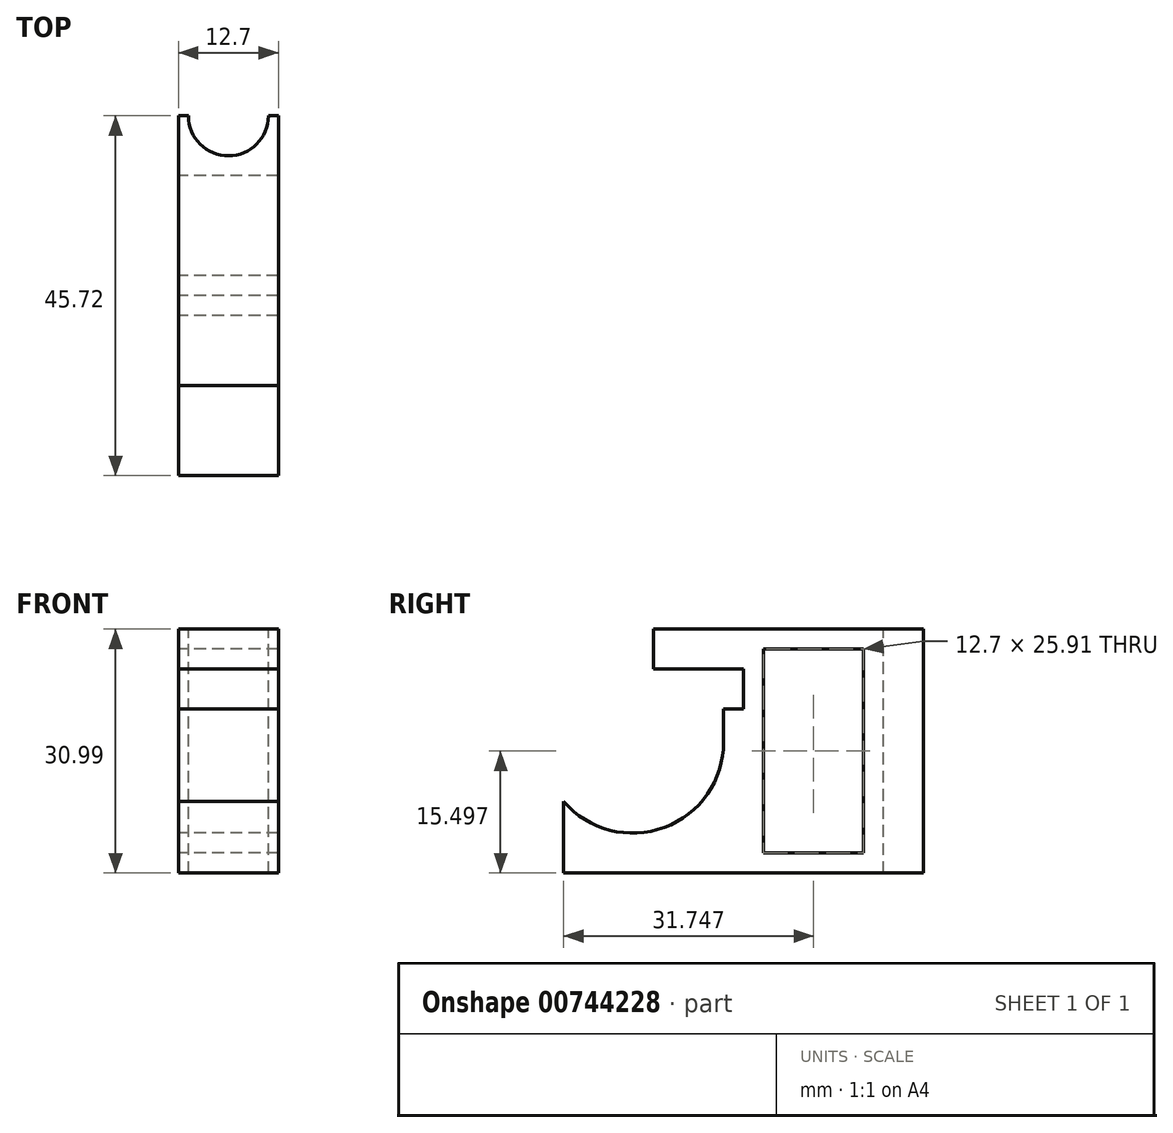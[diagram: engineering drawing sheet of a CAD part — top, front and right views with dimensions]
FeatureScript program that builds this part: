
annotation { "Feature Type Name" : "Feature", "Feature Type Description" : "" }
export const myFeature = defineFeature(function(context is Context, id is Id, definition is map)
    precondition{}
    {
        {
            var Q0;
            Q0=qCreatedBy(makeId("Right.planeOp"),FACE);
            var sketch = newSketch(context, id + "F0", { "sketchPlane" : qUnion([Q0])});
            skArc(sketch, "E0", {"start": v(-8.76, -7.53) * mm, "mid": v(4.02, -10.84) * mm, "end": v(11.56, 0) * mm});
            skLineSegment(sketch, "E1", {"start": v(-8.76, -7.53) * mm, "end": v(-8.76, -16.64) * mm});
            skLineSegment(sketch, "E2", {"start": v(-8.76, -16.64) * mm, "end": v(11.56, -16.64) * mm});
            skLineSegment(sketch, "E3", {"start": v(11.56, 0) * mm, "end": v(11.56, 4.2) * mm});
            skLineSegment(sketch, "E4", {"start": v(11.56, 4.2) * mm, "end": v(14.1, 4.2) * mm});
            skLineSegment(sketch, "E5", {"start": v(14.1, 4.2) * mm, "end": v(14.1, 9.27) * mm});
            skLineSegment(sketch, "E6", {"start": v(14.1, 9.27) * mm, "end": v(11.56, 9.27) * mm});
            skLineSegment(sketch, "E7", {"start": v(11.56, 9.27) * mm, "end": v(2.67, 9.27) * mm});
            skLineSegment(sketch, "E8", {"start": v(2.67, 9.27) * mm, "end": v(2.67, 14.35) * mm});
            skLineSegment(sketch, "E9", {"start": v(2.67, 14.35) * mm, "end": v(16.64, 14.35) * mm});
            skLineSegment(sketch, "E10", {"start": v(16.64, 14.35) * mm, "end": v(16.64, -16.64) * mm});
            skLineSegment(sketch, "E11", {"start": v(16.64, -16.64) * mm, "end": v(11.56, -16.64) * mm});
            skSolve(sketch);
        }
        {
            var Q0;
            Q0=makeQuery(id+"F0.imprint","IMPRINT",FACE,{"disambiguationData":[TD([[makeQuery(id+"F0.imprint","IMPRINT",EDGE,{"derivedFrom":sQuery(id+"F0.wireOp",EDGE,"E0")}),-1.0]])]});
            extrude(context, id + "F1", {"entities" : qUnion([Q0]), "depth" : 12.7 * mm, "offsetDistance" : 25.4 * mm});
        }
        {
            var Q0;
            Q0=makeQuery(id+"F1.opExtrude","CAP_FACE",FACE,{"disambiguationData":[OSD([sQuery(id+"F0.wireOp",EDGE,"E0"),sQuery(id+"F0.wireOp",EDGE,"E1"),sQuery(id+"F0.wireOp",EDGE,"E2"),sQuery(id+"F0.wireOp",EDGE,"E3"),sQuery(id+"F0.wireOp",EDGE,"E4"),sQuery(id+"F0.wireOp",EDGE,"E5"),sQuery(id+"F0.wireOp",EDGE,"E6"),sQuery(id+"F0.wireOp",EDGE,"E7"),sQuery(id+"F0.wireOp",EDGE,"E8"),sQuery(id+"F0.wireOp",EDGE,"E9"),sQuery(id+"F0.wireOp",EDGE,"E10"),sQuery(id+"F0.wireOp",EDGE,"E11")])],"isStart":true});
            var sketch = newSketch(context, id + "F2", { "sketchPlane" : qUnion([Q0])});
            skLineSegment(sketch, "E12", {"start": v(-16.64, 14.35) * mm, "end": v(-36.96, 14.35) * mm});
            skLineSegment(sketch, "E13", {"start": v(-36.96, 14.35) * mm, "end": v(-36.96, -16.64) * mm});
            skLineSegment(sketch, "E14", {"start": v(-36.96, -16.64) * mm, "end": v(-16.64, -16.64) * mm});
            skLineSegment(sketch, "E15", {"start": v(-16.64, -16.64) * mm, "end": v(-16.64, -14.1) * mm});
            skLineSegment(sketch, "E16", {"start": v(-16.64, -14.1) * mm, "end": v(-29.34, -14.1) * mm});
            skLineSegment(sketch, "E17", {"start": v(-29.34, -14.1) * mm, "end": v(-29.34, 11.81) * mm});
            skLineSegment(sketch, "E18", {"start": v(-29.34, 11.81) * mm, "end": v(-16.64, 11.81) * mm});
            skSolve(sketch);
        }
        {
            var Q0;
            {var subQ0=sQuery(id+"F2.wireOp",EDGE,"E12");Q0=makeQuery(id+"F2.imprint","IMPRINT",FACE,{"disambiguationData":[TD([[makeQuery(id+"F2.imprint","IMPRINT",EDGE,{"derivedFrom":subQ0}),1.0]])]});}
            extrude(context, id + "F3", {"entities" : qUnion([Q0]), "operationType" : NewBodyOperationType.ADD, "oppositeDirection" : true, "depth" : 12.7 * mm, "offsetDistance" : 25.4 * mm});
        }
        {
            var Q0;
            Q0=makeQuery(id+"F3.boolean.opBoolean","MERGE",FACE,{"derivedFrom":[makeQuery(id+"F1.opExtrude","SWEPT_FACE",FACE,{"disambiguationData":[OSD([sQuery(id+"F0.wireOp",EDGE,"E9")])]}),makeQuery(id+"F3.opExtrude","SWEPT_FACE",FACE,{"disambiguationData":[OSD([sQuery(id+"F2.wireOp",EDGE,"E12")])]})]});
            var sketch = newSketch(context, id + "F4", { "sketchPlane" : qUnion([Q0])});
            skCircle(sketch, "E19", {"center": v(6.35, 36.96) * mm, "radius": 5.08 * mm});
            skSolve(sketch);
        }
        {
            var Q0;
            {var subQ0=sQuery(id+"F4.wireOp",EDGE,"E19");var subQ1=makeQuery(id+"F3.opExtrude","SWEPT_EDGE",EDGE,{"disambiguationData":[OSD([sQuery(id+"F2.wireOp",EDGE,"E12"),sQuery(id+"F2.wireOp",EDGE,"E13")])]});var subQ2=makeQuery(id+"F4.imprint","INTERSECT",VERTEX,{"disambiguationData":[OD(0.0)],"derivedFrom":[subQ1,subQ0]});Q0=makeQuery(id+"F4.imprint","IMPRINT",FACE,{"disambiguationData":[TD([[makeQuery(id+"F4.imprint","IMPRINT",EDGE,{"disambiguationData":[TD([[subQ2,-1.0]])],"derivedFrom":subQ0}),1.0]])]});}
            var Q1;
            {var subQ0=sQuery(id+"F4.wireOp",EDGE,"E19");var subQ1=makeQuery(id+"F3.opExtrude","SWEPT_EDGE",EDGE,{"disambiguationData":[OSD([sQuery(id+"F2.wireOp",EDGE,"E12"),sQuery(id+"F2.wireOp",EDGE,"E13")])]});var subQ2=makeQuery(id+"F4.imprint","INTERSECT",VERTEX,{"disambiguationData":[OD(0.0)],"derivedFrom":[subQ1,subQ0]});Q1=makeQuery(id+"F4.imprint","IMPRINT",FACE,{"disambiguationData":[TD([[makeQuery(id+"F4.imprint","IMPRINT",EDGE,{"disambiguationData":[TD([[subQ2,1.0]])],"derivedFrom":subQ0}),1.0]])]});}
            extrude(context, id + "F5", {"entities" : qUnion([Q0, Q1]), "operationType" : NewBodyOperationType.REMOVE, "oppositeDirection" : true, "depth" : 76.2 * mm, "offsetDistance" : 25.4 * mm});
        }
    });
